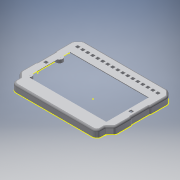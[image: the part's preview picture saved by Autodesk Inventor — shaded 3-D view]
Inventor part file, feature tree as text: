
AUTODESK INVENTOR PART (.ipt)
format: ipt  version: 2017 SP1 (Build 210196100, 196)  size: 1,684,480 bytes
history: native  units: mm
features: other x7, sketch x3, extrude x3, projected_geometry x2, reference x2, fillet x1, plane x1, chamfer x1, shell x1
ambient origin geometry x8: Origin, YZ Plane, XZ Plane, XY Plane, X Axis, Y Axis, Z Axis, Center Point
bodies: Volumenkörper1 (feature_tree), Volumenkörper3 (feature_tree)
feature tree (21):
  other  "GehäuseDeckel"
  other  "Deckel.ipt:1"
  other  "DummyAuschnitt2.ipt:1"
  fillet  "Rundung2"  Radius=10.0mm
  sketch  "Skizze6"  dims[d54=3.0mm d55=10.0mm d56=0.0mm]
  plane  "Arbeitsebene1"
  extrude  "Extrusion5"  Depth=10.0mm TaperAngle=0.0deg
  extrude  "Extrusion6"  Depth=1.0mm
  chamfer  "Fase2"  Distance=10.0mm
  extrude  "Extrusion8"  Depth=10.0mm
  shell  "Wandung1"  Thickness=1.0mm
  projected_geometry  "Projizierte Kontur6"
  reference  "Referenz3"
  sketch  "Skizze7"  dims[d57=1.73mm d58=1.0mm]
  projected_geometry  "Projizierte Kontur7"
  reference  "Referenz4"
  sketch  "Skizze11"  dims[d59=10.0mm d60=1.0mm d61=10.0mm d62=1.0mm d63=10.0mm d64=1.0mm d65=10.0mm d66=1.0mm d67=10.0mm d68=1.0mm d69=10.0mm d70=1.0mm d71=10.0mm d72=1.0mm d73=10.0mm d76=1.0mm d78=10.0mm d79=0.0mm d80=0.3mm d81=2.0mm d82=45.0deg d83=2.0mm d84=2.0mm d87=0.3mm d88=0.0mm d89=0.5mm]
  other  "<userpath>\Dropbox\Elektronik\aXe_Dashboard240XL\Gehäuse\Montiert.iam"
  other  "Montiert.iam"
  other  "PCB_SingleLedRow:1"
  other  "Schnittkanten projizieren2"
